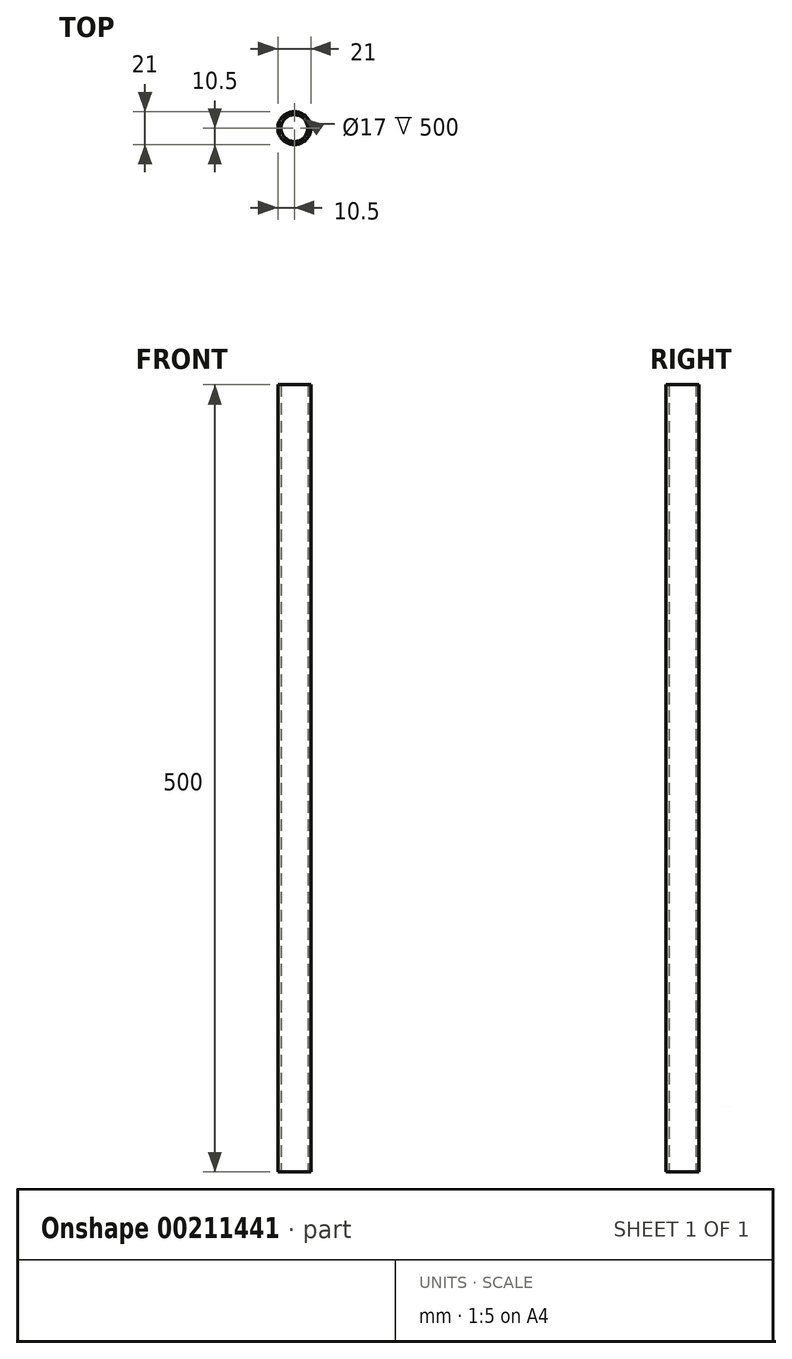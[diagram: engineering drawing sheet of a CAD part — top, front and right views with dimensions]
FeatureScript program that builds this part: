
annotation { "Feature Type Name" : "Feature", "Feature Type Description" : "" }
export const myFeature = defineFeature(function(context is Context, id is Id, definition is map)
    precondition{}
    {
        {
            var Q0;
            Q0=qCreatedBy(makeId("Top.planeOp"),FACE);
            var sketch = newSketch(context, id + "F0", { "sketchPlane" : qUnion([Q0])});
            skCircle(sketch, "E0", {"center": v(0, 0) * mm, "radius": 10.5 * mm});
            skCircle(sketch, "E1", {"center": v(0, 0) * mm, "radius": 8.5 * mm});
            skSolve(sketch);
        }
        {
            var Q0;
            Q0 = qSketchRegion(id + "F0", true);
            extrude(context, id + "F1", {"entities" : qUnion([Q0]), "depth" : 500 * mm});
        }
    });
